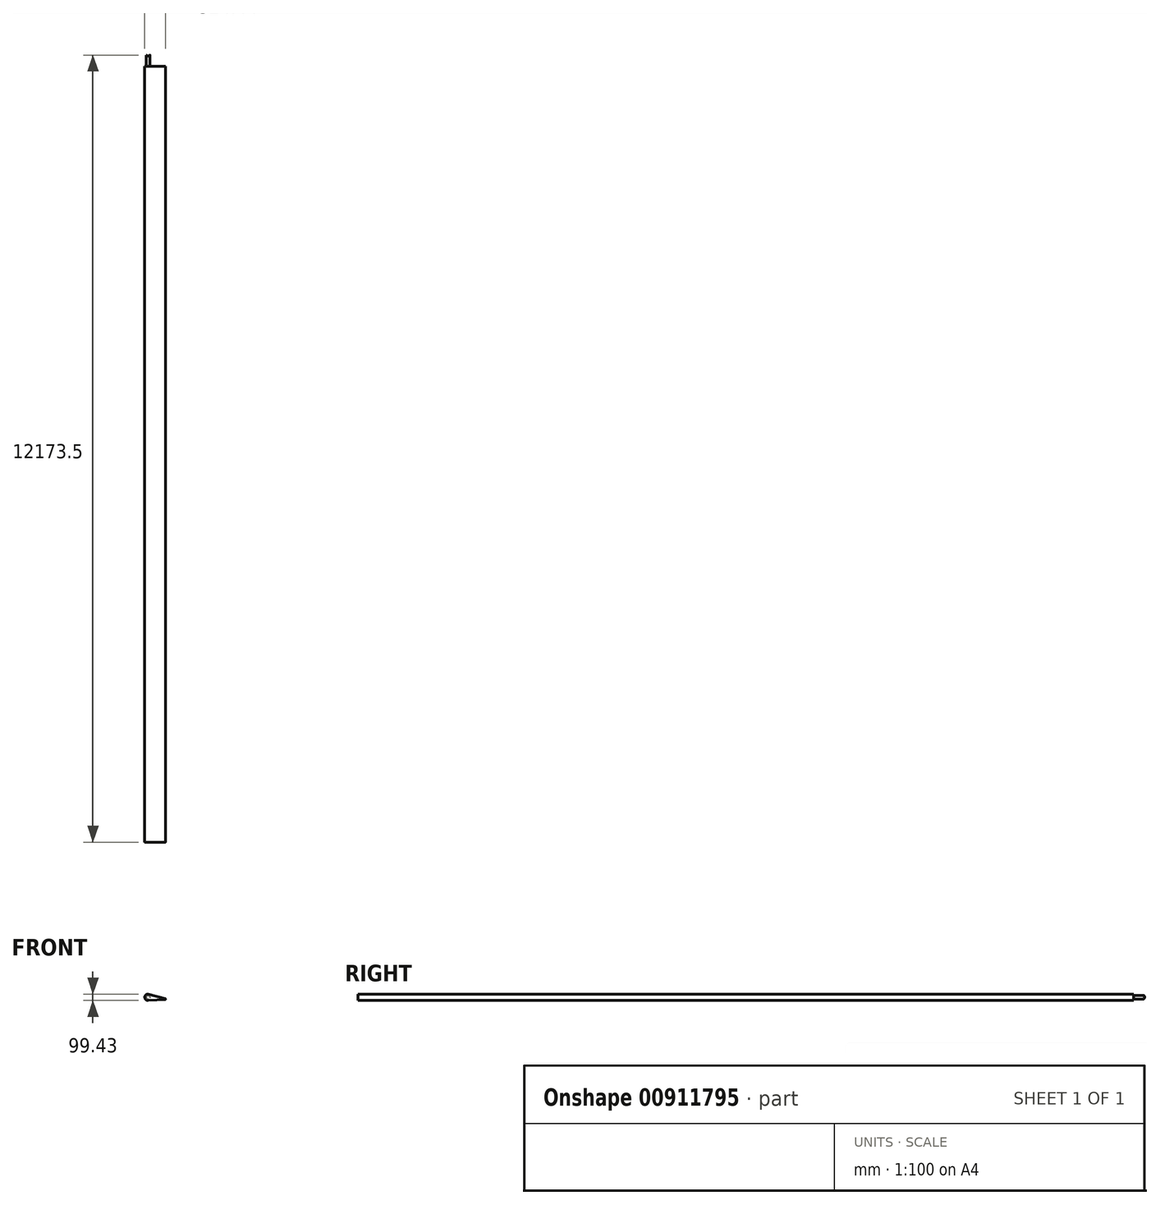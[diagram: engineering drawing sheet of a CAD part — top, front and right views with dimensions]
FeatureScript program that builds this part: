
annotation { "Feature Type Name" : "Feature", "Feature Type Description" : "" }
export const myFeature = defineFeature(function(context is Context, id is Id, definition is map)
    precondition{}
    {
        {
            var Q0;
            Q0=qCreatedBy(makeId("Front.planeOp"),FACE);
            var sketch = newSketch(context, id + "F0", { "sketchPlane" : qUnion([Q0])});
            skLineSegment(sketch, "E0", {"start": v(0, 50) * mm, "end": v(0, -50) * mm});
            skArc(sketch, "E1", {"start": v(0, 50) * mm, "mid": v(-50, 0) * mm, "end": v(0, -50) * mm});
            skLineSegment(sketch, "E2", {"start": v(0, -30) * mm, "end": v(300, -30) * mm});
            skLineSegment(sketch, "E3", {"start": v(0, 50) * mm, "end": v(300, -30) * mm});
            skLineSegment(sketch, "E4", {"start": v(0, -50) * mm, "end": v(300, -30) * mm});
            skSolve(sketch);
        }
        {
            var Q0;
            {var subQ0=sQuery(id+"F0.wireOp",EDGE,"E1");Q0=makeQuery(id+"F0.imprint","IMPRINT",FACE,{"disambiguationData":[TD([[makeQuery(id+"F0.imprint","IMPRINT",EDGE,{"derivedFrom":subQ0}),1.0]])]});}
            var Q1;
            {var subQ2=sQuery(id+"F0.wireOp",EDGE,"E2");Q1=makeQuery(id+"F0.imprint","IMPRINT",FACE,{"disambiguationData":[TD([[makeQuery(id+"F0.imprint","IMPRINT",EDGE,{"derivedFrom":subQ2}),1.0]])]});}
            var Q2;
            {var subQ2=sQuery(id+"F0.wireOp",EDGE,"E2");Q2=makeQuery(id+"F0.imprint","IMPRINT",FACE,{"disambiguationData":[TD([[makeQuery(id+"F0.imprint","IMPRINT",EDGE,{"derivedFrom":subQ2}),-1.0]])]});}
            extrude(context, id + "F1", {"entities" : qUnion([Q0, Q1, Q2]), "depth" : 12000 * mm, "offsetDistance" : 25 * mm});
        }
        {
            var Q0;
            Q0=makeQuery(id+"F1.opExtrude","SWEPT_EDGE",EDGE,{"disambiguationData":[OSD([sQuery(id+"F0.wireOp",EDGE,"E0"),sQuery(id+"F0.wireOp",EDGE,"E1"),sQuery(id+"F0.wireOp",EDGE,"E3")])]});
            var Q1;
            Q1=makeQuery(id+"F1.opExtrude","SWEPT_EDGE",EDGE,{"disambiguationData":[OSD([sQuery(id+"F0.wireOp",EDGE,"E0"),sQuery(id+"F0.wireOp",EDGE,"E1"),sQuery(id+"F0.wireOp",EDGE,"E4")])]});
            fillet(context, id + "F2", {"entities" : qUnion([Q0, Q1]), "radius" : 40 * mm, "tangentPropagation" : true, "allowEdgeOverflow" : false});
        }
        {
            var Q0;
            Q0=makeQuery(id+"F1.opExtrude","SWEPT_EDGE",EDGE,{"disambiguationData":[OSD([sQuery(id+"F0.wireOp",EDGE,"E2"),sQuery(id+"F0.wireOp",EDGE,"E3"),sQuery(id+"F0.wireOp",EDGE,"E4")])]});
            fillet(context, id + "F3", {"entities" : qUnion([Q0]), "radius" : 5 * mm, "tangentPropagation" : true, "allowEdgeOverflow" : false});
        }
        {
            var Q0;
            Q0=qCreatedBy(makeId("Front.planeOp"),FACE);
            var sketch = newSketch(context, id + "F4", { "sketchPlane" : qUnion([Q0])});
            skCircle(sketch, "E5", {"center": v(0, 0) * mm, "radius": 30 * mm});
            skSolve(sketch);
        }
        {
            var Q0;
            Q0=qSketchRegion(id+"F4",true);
            extrude(context, id + "F5", {"entities" : qUnion([Q0]), "operationType" : NewBodyOperationType.ADD, "oppositeDirection" : true, "depth" : 200 * mm, "offsetDistance" : 25 * mm});
        }
        {
            var Q0;
            Q0=qCreatedBy(makeId("Top.planeOp"),FACE);
            var sketch = newSketch(context, id + "F6", { "sketchPlane" : qUnion([Q0])});
            skLineSegment(sketch, "E6", {"start": v(0, 0) * mm, "end": v(0, 200) * mm});
            skCircle(sketch, "E7", {"center": v(0, 200) * mm, "radius": 40 * mm});
            skSolve(sketch);
        }
        {
            var Q0;
            Q0=makeQuery(id+"F6.imprint","IMPRINT",FACE,{"disambiguationData":[TD([[makeQuery(id+"F6.imprint","IMPRINT",EDGE,{"derivedFrom":sQuery(id+"F6.wireOp",EDGE,"E7")}),1.0]])]});
            extrude(context, id + "F7", {"entities" : qUnion([Q0]), "operationType" : NewBodyOperationType.REMOVE, "oppositeDirection" : true, "depth" : 100 * mm, "offsetDistance" : 25 * mm, "symmetric" : true});
        }
    });
